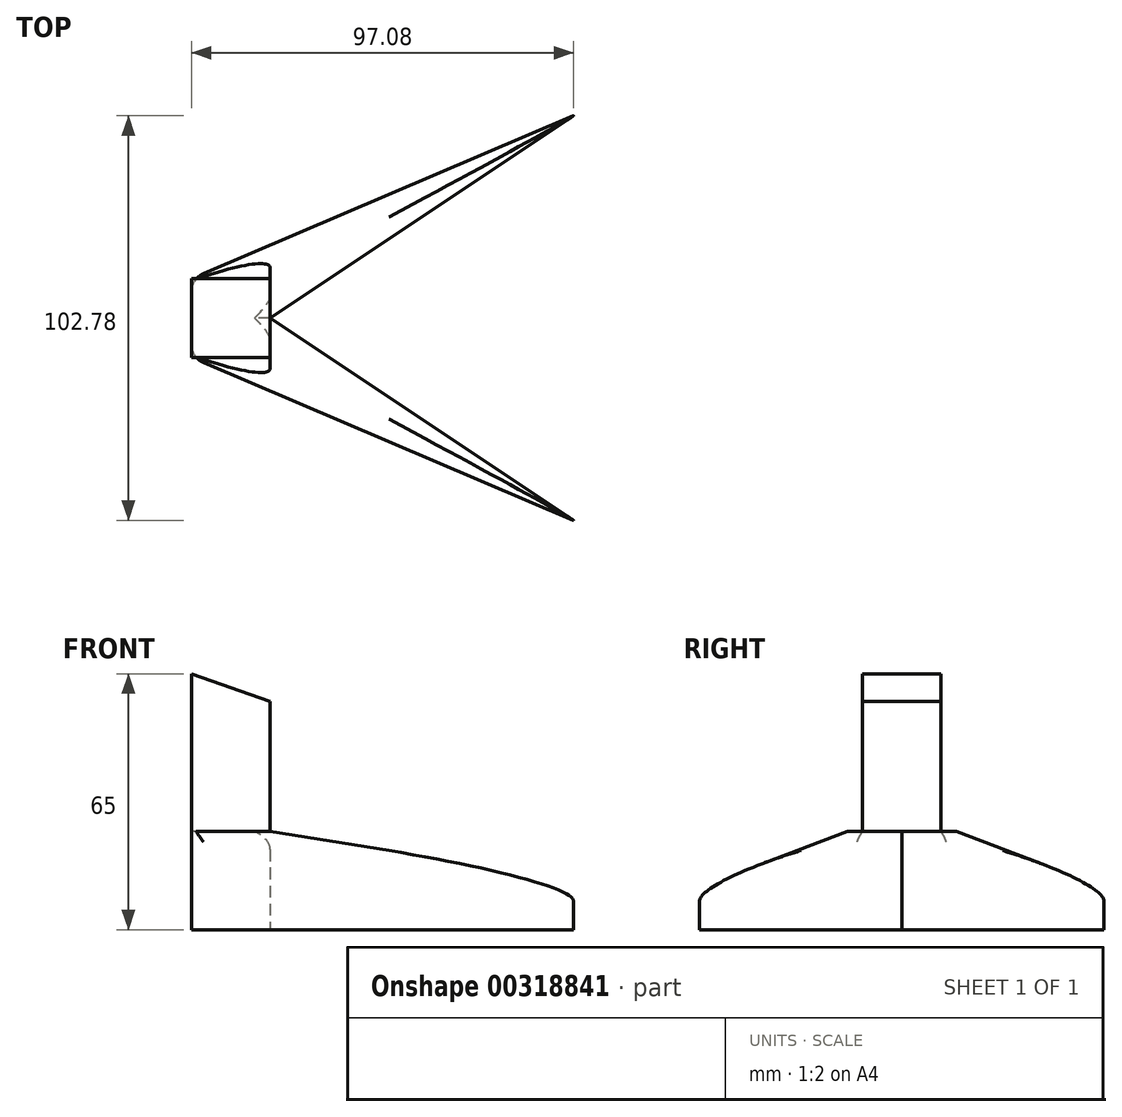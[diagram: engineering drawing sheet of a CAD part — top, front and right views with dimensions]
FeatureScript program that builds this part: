
annotation { "Feature Type Name" : "Feature", "Feature Type Description" : "" }
export const myFeature = defineFeature(function(context is Context, id is Id, definition is map)
    precondition{}
    {
        {
            var Q0;
            Q0=qCreatedBy(makeId("Top.planeOp"),FACE);
            var sketch = newSketch(context, id + "F0", { "sketchPlane" : qUnion([Q0])});
            skLineSegment(sketch, "E0.bottom", {"start": v(10, 10) * mm, "end": v(-10, 10) * mm});
            skLineSegment(sketch, "E0.top", {"start": v(10, -10) * mm, "end": v(-10, -10) * mm});
            skLineSegment(sketch, "E0.left", {"start": v(10, 10) * mm, "end": v(10, -10) * mm});
            skLineSegment(sketch, "E0.right", {"start": v(-10, 10) * mm, "end": v(-10, -10) * mm});
            skPoint(sketch, "E0.middle", {"position": v(0, 0) * mm});
            skLineSegment(sketch, "E1", {"start": v(-10, 10) * mm, "end": v(87.08, 51.4) * mm});
            skLineSegment(sketch, "E2", {"start": v(87.08, 51.4) * mm, "end": v(10, 0) * mm});
            skLineSegment(sketch, "E3.MirrorCS", {"start": v(87.08, -51.4) * mm, "end": v(10, 0) * mm});
            skLineSegment(sketch, "E4.MirrorCS", {"start": v(-10, -10) * mm, "end": v(87.08, -51.4) * mm});
            skSolve(sketch);
        }
        {
            var Q0;
            {var subQ0=sQuery(id+"F0.wireOp",EDGE,"E0.top");Q0=makeQuery(id+"F0.imprint","IMPRINT",FACE,{"disambiguationData":[TD([[makeQuery(id+"F0.imprint","IMPRINT",EDGE,{"derivedFrom":subQ0}),1.0]])]});}
            var Q1;
            {var subQ3=sQuery(id+"F0.wireOp",EDGE,"E0.bottom");Q1=makeQuery(id+"F0.imprint","IMPRINT",FACE,{"disambiguationData":[TD([[makeQuery(id+"F0.imprint","IMPRINT",EDGE,{"derivedFrom":subQ3}),1.0]])]});}
            var Q2;
            {var subQ0=sQuery(id+"F0.wireOp",EDGE,"E0.bottom");Q2=makeQuery(id+"F0.imprint","IMPRINT",FACE,{"disambiguationData":[TD([[makeQuery(id+"F0.imprint","IMPRINT",EDGE,{"derivedFrom":subQ0}),-1.0]])]});}
            extrude(context, id + "F1", {"entities" : qUnion([Q0, Q1, Q2]), "depth" : 20 * mm});
        }
        {
            var Q0;
            Q0 = qSketchRegion(id + "F0", true);
            extrude(context, id + "F2", {"entities" : qUnion([Q0]), "operationType" : NewBodyOperationType.ADD, "depth" : 25 * mm});
        }
        {
            var Q0;
            Q0=makeQuery(id+"F2.opExtrude","CAP_FACE",FACE,{"disambiguationData":[OSD([sQuery(id+"F0.wireOp",EDGE,"E0.right"),sQuery(id+"F0.wireOp",EDGE,"E1"),sQuery(id+"F0.wireOp",EDGE,"E2"),sQuery(id+"F0.wireOp",EDGE,"E3.MirrorCS"),sQuery(id+"F0.wireOp",EDGE,"E4.MirrorCS")])],"isStart":false});
            var sketch = newSketch(context, id + "F3", { "sketchPlane" : qUnion([Q0])});
            skLineSegment(sketch, "E5.bottom", {"start": v(-10, 10) * mm, "end": v(10, 10) * mm});
            skLineSegment(sketch, "E5.top", {"start": v(-10, -10) * mm, "end": v(10, -10) * mm});
            skLineSegment(sketch, "E5.left", {"start": v(-10, 10) * mm, "end": v(-10, -10) * mm});
            skLineSegment(sketch, "E5.right", {"start": v(10, 10) * mm, "end": v(10, -10) * mm});
            skPoint(sketch, "E5.middle", {"position": v(0, 0) * mm});
            skSolve(sketch);
        }
        {
            var Q0;
            {var subQ2=sQuery(id+"F3.wireOp",EDGE,"E5.bottom");Q0=makeQuery(id+"F3.imprint","IMPRINT",FACE,{"disambiguationData":[TD([[makeQuery(id+"F3.imprint","IMPRINT",EDGE,{"derivedFrom":subQ2}),-1.0]])]});}
            extrude(context, id + "F4", {"entities" : qUnion([Q0]), "depth" : 40 * mm});
        }
        {
            var Q0;
            Q0=makeQuery(id+"F4.opExtrude","SWEPT_FACE",FACE,{"disambiguationData":[OSD([sQuery(id+"F3.wireOp",EDGE,"E5.top")])]});
            var sketch = newSketch(context, id + "F5", { "sketchPlane" : qUnion([Q0])});
            skLineSegment(sketch, "E6", {"start": v(-10, 65) * mm, "end": v(10, 65) * mm});
            skLineSegment(sketch, "E7", {"start": v(10, 65) * mm, "end": v(10, 58) * mm});
            skLineSegment(sketch, "E8", {"start": v(10, 58) * mm, "end": v(-10, 65) * mm});
            skSolve(sketch);
        }
        {
            var Q0;
            Q0 = qSketchRegion(id + "F5", true);
            extrude(context, id + "F6", {"entities" : qUnion([Q0]), "operationType" : NewBodyOperationType.REMOVE, "endBound" : BoundingType.THROUGH_ALL, "oppositeDirection" : true, "depth" : 25 * mm});
        }
        {
            var Q0;
            Q0=qCreatedBy(makeId("Front.planeOp"),FACE);
            var sketch = newSketch(context, id + "F7", { "sketchPlane" : qUnion([Q0])});
            skLineSegment(sketch, "E9.0.0", {"start": v(-10, 0) * mm, "end": v(87.08, 0) * mm, "construction": true});
            skLineSegment(sketch, "E9.0.1", {"start": v(87.08, 0) * mm, "end": v(87.08, 25) * mm, "construction": true});
            skLineSegment(sketch, "E9.0.2", {"start": v(87.08, 25) * mm, "end": v(-10, 25) * mm, "construction": true});
            skLineSegment(sketch, "E9.0.3", {"start": v(-10, 25) * mm, "end": v(-10, 0) * mm, "construction": true});
            skLineSegment(sketch, "E10.0.0", {"start": v(10, 25) * mm, "end": v(10, 58) * mm, "construction": true});
            skLineSegment(sketch, "E10.0.1", {"start": v(10, 58) * mm, "end": v(-10, 65) * mm, "construction": true});
            skLineSegment(sketch, "E10.0.2", {"start": v(-10, 65) * mm, "end": v(-10, 25) * mm, "construction": true});
            skLineSegment(sketch, "E10.0.3", {"start": v(-10, 25) * mm, "end": v(10, 25) * mm, "construction": true});
            skLineSegment(sketch, "E11", {"start": v(10, 25) * mm, "end": v(87.08, 12.5) * mm});
            skLineSegment(sketch, "E12", {"start": v(87.08, 12.5) * mm, "end": v(87.08, 25) * mm});
            skLineSegment(sketch, "E13", {"start": v(10, 25) * mm, "end": v(87.08, 25) * mm});
            skSolve(sketch);
        }
        {
            var Q0;
            Q0 = qSketchRegion(id + "F7", true);
            extrude(context, id + "F8", {"entities" : qUnion([Q0]), "operationType" : NewBodyOperationType.REMOVE, "endBound" : BoundingType.SYMMETRIC, "depth" : 169.2 * mm});
        }
        {
            var Q0;
            {var subQ0=sQuery(id+"F0.wireOp",EDGE,"E4.MirrorCS");Q0=makeQuery(id+"F8.boolean.opBoolean","INTERSECT",EDGE,{"derivedFrom":[makeQuery(id+"F2.boolean.opBoolean","MERGE",FACE,{"derivedFrom":[makeQuery(id+"F1.opExtrude","SWEPT_FACE",FACE,{"disambiguationData":[OSD([subQ0])]}),makeQuery(id+"F2.opExtrude","SWEPT_FACE",FACE,{"disambiguationData":[OSD([subQ0])]})]}),makeQuery(id+"F8.opExtrude","SWEPT_FACE",FACE,{"disambiguationData":[OSD([sQuery(id+"F7.wireOp",EDGE,"E11")])]})]});}
            var Q1;
            {var subQ0=sQuery(id+"F0.wireOp",EDGE,"E3.MirrorCS");Q1=makeQuery(id+"F8.boolean.opBoolean","INTERSECT",EDGE,{"derivedFrom":[makeQuery(id+"F2.boolean.opBoolean","MERGE",FACE,{"derivedFrom":[makeQuery(id+"F1.opExtrude","SWEPT_FACE",FACE,{"disambiguationData":[OSD([subQ0])]}),makeQuery(id+"F2.opExtrude","SWEPT_FACE",FACE,{"disambiguationData":[OSD([subQ0])]})]}),makeQuery(id+"F8.opExtrude","SWEPT_FACE",FACE,{"disambiguationData":[OSD([sQuery(id+"F7.wireOp",EDGE,"E11")])]})]});}
            fillet(context, id + "F9", {"entities" : qUnion([Q0, Q1]), "radius" : 5 * mm, "tangentPropagation" : true, "allowEdgeOverflow" : false});
        }
        {
            var Q0;
            {var subQ0=sQuery(id+"F0.wireOp",EDGE,"E2");Q0=makeQuery(id+"F8.boolean.opBoolean","INTERSECT",EDGE,{"derivedFrom":[makeQuery(id+"F2.boolean.opBoolean","MERGE",FACE,{"derivedFrom":[makeQuery(id+"F1.opExtrude","SWEPT_FACE",FACE,{"disambiguationData":[OSD([subQ0])]}),makeQuery(id+"F2.opExtrude","SWEPT_FACE",FACE,{"disambiguationData":[OSD([subQ0])]})]}),makeQuery(id+"F8.opExtrude","SWEPT_FACE",FACE,{"disambiguationData":[OSD([sQuery(id+"F7.wireOp",EDGE,"E11")])]})]});}
            var Q1;
            {var subQ0=sQuery(id+"F0.wireOp",EDGE,"E1");Q1=makeQuery(id+"F8.boolean.opBoolean","INTERSECT",EDGE,{"derivedFrom":[makeQuery(id+"F2.boolean.opBoolean","MERGE",FACE,{"derivedFrom":[makeQuery(id+"F1.opExtrude","SWEPT_FACE",FACE,{"disambiguationData":[OSD([subQ0])]}),makeQuery(id+"F2.opExtrude","SWEPT_FACE",FACE,{"disambiguationData":[OSD([subQ0])]})]}),makeQuery(id+"F8.opExtrude","SWEPT_FACE",FACE,{"disambiguationData":[OSD([sQuery(id+"F7.wireOp",EDGE,"E11")])]})]});}
            fillet(context, id + "F10", {"entities" : qUnion([Q0, Q1]), "radius" : 5 * mm, "tangentPropagation" : true, "allowEdgeOverflow" : false});
        }
        {
            var Q0;
            {var subQ0=sQuery(id+"F0.wireOp",EDGE,"E4.MirrorCS");var subQ1=sQuery(id+"F0.wireOp",EDGE,"E0.right");var subQ2=sQuery(id+"F0.wireOp",EDGE,"E0.top");Q0=makeQuery(id+"F2.boolean.opBoolean","MERGE",EDGE,{"derivedFrom":[makeQuery(id+"F1.opExtrude","SWEPT_EDGE",EDGE,{"disambiguationData":[OSD([subQ2,subQ1,subQ0])]}),makeQuery(id+"F2.opExtrude","SWEPT_EDGE",EDGE,{"disambiguationData":[OSD([subQ2,subQ1,subQ0])]})]});}
            var Q1;
            {var subQ0=sQuery(id+"F0.wireOp",EDGE,"E1");var subQ1=sQuery(id+"F0.wireOp",EDGE,"E0.right");var subQ2=sQuery(id+"F0.wireOp",EDGE,"E0.bottom");Q1=makeQuery(id+"F2.boolean.opBoolean","MERGE",EDGE,{"derivedFrom":[makeQuery(id+"F1.opExtrude","SWEPT_EDGE",EDGE,{"disambiguationData":[OSD([subQ2,subQ1,subQ0])]}),makeQuery(id+"F2.opExtrude","SWEPT_EDGE",EDGE,{"disambiguationData":[OSD([subQ2,subQ1,subQ0])]})]});}
            fillet(context, id + "F11", {"entities" : qUnion([Q0, Q1]), "radius" : 5 * mm, "tangentPropagation" : true, "allowEdgeOverflow" : false});
        }
    });
